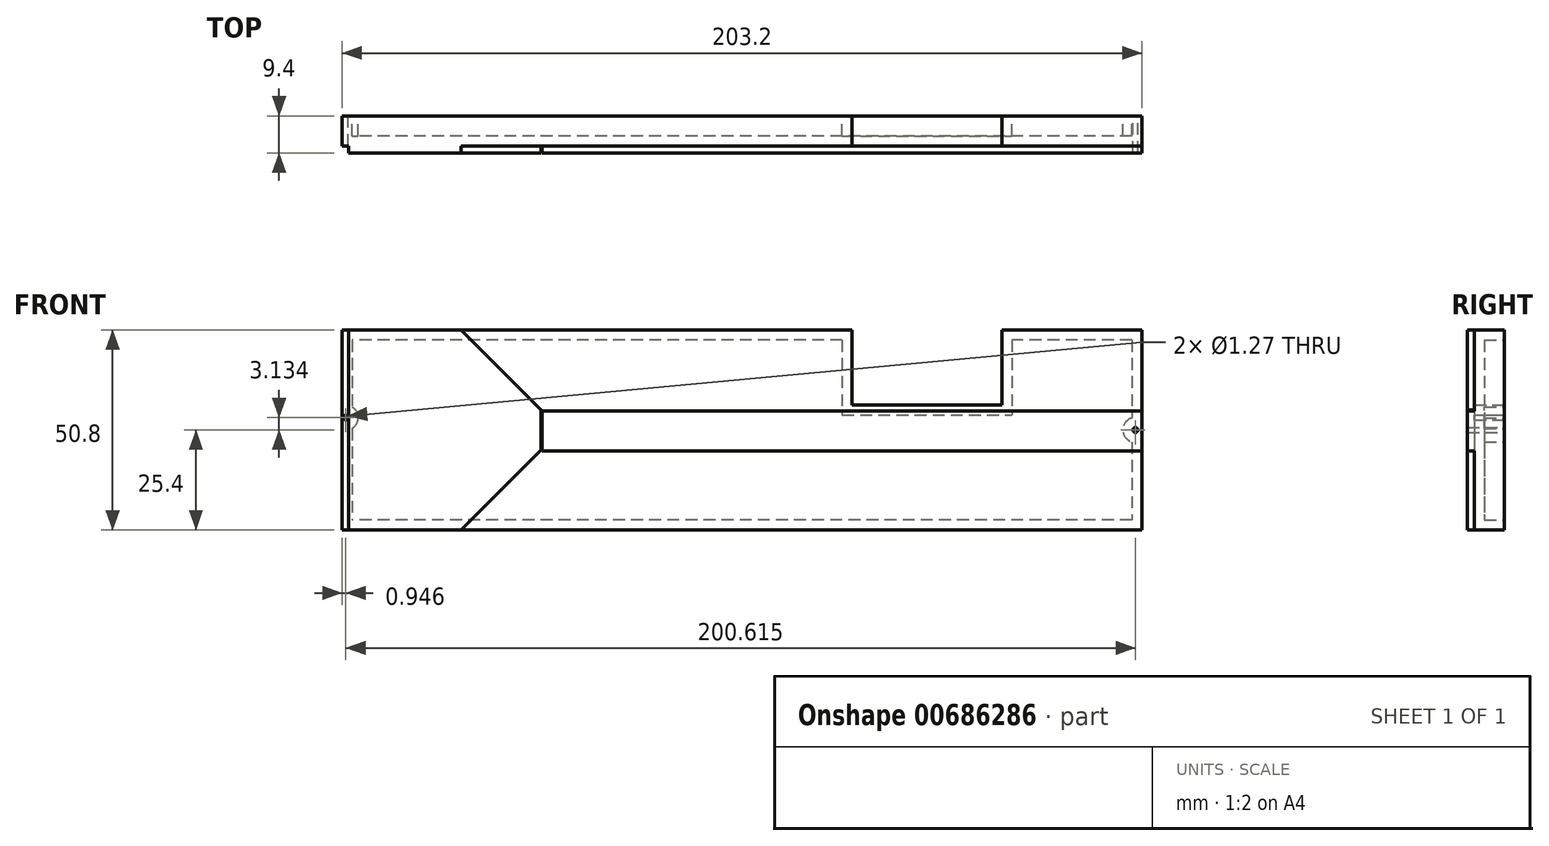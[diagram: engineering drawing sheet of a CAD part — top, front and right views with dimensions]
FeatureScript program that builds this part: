
annotation { "Feature Type Name" : "Feature", "Feature Type Description" : "" }
export const myFeature = defineFeature(function(context is Context, id is Id, definition is map)
    precondition{}
    {
        {
            var Q0;
            Q0=qCreatedBy(makeId("Front.planeOp"),FACE);
            var sketch = newSketch(context, id + "F0", { "sketchPlane" : qUnion([Q0])});
            skLineSegment(sketch, "E0.bottom", {"start": v(101.6, 25.4) * mm, "end": v(-101.6, 25.4) * mm});
            skLineSegment(sketch, "E0.top", {"start": v(101.6, -25.4) * mm, "end": v(-101.6, -25.4) * mm});
            skLineSegment(sketch, "E0.left", {"start": v(101.6, 25.4) * mm, "end": v(101.6, -25.4) * mm});
            skLineSegment(sketch, "E0.right", {"start": v(-101.6, 25.4) * mm, "end": v(-101.6, -25.4) * mm});
            skPoint(sketch, "E0.middle", {"position": v(0, 0) * mm});
            skLineSegment(sketch, "E1.bottom", {"start": v(28.01, 25.4) * mm, "end": v(66.11, 25.4) * mm});
            skLineSegment(sketch, "E1.top", {"start": v(28.01, 6.35) * mm, "end": v(66.11, 6.35) * mm});
            skLineSegment(sketch, "E1.left", {"start": v(28.01, 25.4) * mm, "end": v(28.01, 6.35) * mm});
            skLineSegment(sketch, "E1.right", {"start": v(66.11, 25.4) * mm, "end": v(66.11, 6.35) * mm});
            skCircle(sketch, "E2", {"center": v(-100.65, 3.13) * mm, "radius": 0.64 * mm});
            skCircle(sketch, "E3", {"center": v(99.96, 0) * mm, "radius": 0.64 * mm});
            skPoint(sketch, "E3.centerSnap0", {"position": v(101.6, 0) * mm});
            skSolve(sketch);
        }
        {
            var Q0;
            Q0=makeQuery(id+"F0.imprint","IMPRINT",FACE,{"disambiguationData":[TD([[makeQuery(id+"F0.imprint","IMPRINT",EDGE,{"derivedFrom":sQuery(id+"F0.wireOp",EDGE,"E0.bottom")}),1.0]])]});
            extrude(context, id + "F1", {"entities" : qUnion([Q0]), "endBound" : BoundingType.SYMMETRIC, "depth" : 7.62 * mm, "offsetDistance" : 25.4 * mm});
        }
        {
            var Q0;
            Q0=makeQuery(id+"F1.opExtrude","CAP_FACE",FACE,{"disambiguationData":[OSD([sQuery(id+"F0.wireOp",EDGE,"E0.bottom"),sQuery(id+"F0.wireOp",EDGE,"E0.top"),sQuery(id+"F0.wireOp",EDGE,"E0.left"),sQuery(id+"F0.wireOp",EDGE,"E0.right")])],"isStart":true});
            shell(context, id + "F2", {"entities" : qUnion([Q0]), "thickness" : 2.54 * mm});
        }
        {
            var Q0;
            Q0=makeQuery(id+"F1.opExtrude","CAP_FACE",FACE,{"disambiguationData":[OSD([sQuery(id+"F0.wireOp",EDGE,"E0.bottom"),sQuery(id+"F0.wireOp",EDGE,"E0.top"),sQuery(id+"F0.wireOp",EDGE,"E0.left"),sQuery(id+"F0.wireOp",EDGE,"E0.right"),sQuery(id+"F0.wireOp",EDGE,"E1.top"),sQuery(id+"F0.wireOp",EDGE,"E1.left"),sQuery(id+"F0.wireOp",EDGE,"E1.right")])],"isStart":false});
            var sketch = newSketch(context, id + "F3", { "sketchPlane" : qUnion([Q0])});
            skLineSegment(sketch, "E4.bottom", {"start": v(101.6, 4.86) * mm, "end": v(-50.8, 4.86) * mm});
            skLineSegment(sketch, "E4.top", {"start": v(101.6, -5.3) * mm, "end": v(-50.8, -5.3) * mm});
            skLineSegment(sketch, "E4.left", {"start": v(101.6, 4.86) * mm, "end": v(101.6, -5.3) * mm});
            skLineSegment(sketch, "E4.right", {"start": v(-50.8, 4.86) * mm, "end": v(-50.8, -5.3) * mm});
            skSolve(sketch);
        }
        {
            var Q0;
            Q0=makeQuery(id+"F3.imprint","IMPRINT",FACE,{"disambiguationData":[TD([[makeQuery(id+"F3.imprint","IMPRINT",EDGE,{"derivedFrom":sQuery(id+"F3.wireOp",EDGE,"E4.bottom")}),1.0]])]});
            extrude(context, id + "F4", {"entities" : qUnion([Q0]), "operationType" : NewBodyOperationType.ADD, "depth" : 1.78 * mm, "offsetDistance" : 25.4 * mm});
        }
        {
            var Q0;
            Q0=makeQuery(id+"F1.opExtrude","CAP_FACE",FACE,{"disambiguationData":[OSD([sQuery(id+"F0.wireOp",EDGE,"E0.bottom"),sQuery(id+"F0.wireOp",EDGE,"E0.top"),sQuery(id+"F0.wireOp",EDGE,"E0.left"),sQuery(id+"F0.wireOp",EDGE,"E0.right"),sQuery(id+"F0.wireOp",EDGE,"E1.top"),sQuery(id+"F0.wireOp",EDGE,"E1.left"),sQuery(id+"F0.wireOp",EDGE,"E1.right")])],"isStart":false});
            var sketch = newSketch(context, id + "F5", { "sketchPlane" : qUnion([Q0])});
            skLineSegment(sketch, "E5.bottom", {"start": v(-51, 25.4) * mm, "end": v(-99.9, 25.4) * mm});
            skLineSegment(sketch, "E5.top", {"start": v(-51, -25.4) * mm, "end": v(-99.9, -25.4) * mm});
            skLineSegment(sketch, "E5.left", {"start": v(-51, 25.4) * mm, "end": v(-51, -25.4) * mm});
            skLineSegment(sketch, "E5.right", {"start": v(-99.9, 25.4) * mm, "end": v(-99.9, -25.4) * mm});
            skSolve(sketch);
        }
        {
            var Q0;
            Q0=makeQuery(id+"F5.imprint","IMPRINT",FACE,{"disambiguationData":[TD([[makeQuery(id+"F5.imprint","IMPRINT",EDGE,{"derivedFrom":sQuery(id+"F5.wireOp",EDGE,"E5.bottom")}),1.0]])]});
            extrude(context, id + "F6", {"entities" : qUnion([Q0]), "operationType" : NewBodyOperationType.ADD, "depth" : 1.78 * mm, "offsetDistance" : 25.4 * mm});
        }
        {
            var Q0;
            Q0=makeQuery(id+"F6.opExtrude","SWEPT_EDGE",EDGE,{"disambiguationData":[OSD([sQuery(id+"F0.wireOp",EDGE,"E0.bottom"),sQuery(id+"F5.wireOp",EDGE,"E5.bottom"),sQuery(id+"F5.wireOp",EDGE,"E5.left")])]});
            var Q1;
            Q1=makeQuery(id+"F6.opExtrude","SWEPT_EDGE",EDGE,{"disambiguationData":[OSD([sQuery(id+"F0.wireOp",EDGE,"E0.top"),sQuery(id+"F5.wireOp",EDGE,"E5.top"),sQuery(id+"F5.wireOp",EDGE,"E5.left")])]});
            chamfer(context, id + "F7", {"entities" : qUnion([Q0, Q1]), "width" : 20.32 * mm, "tangentPropagation" : true});
        }
    });
